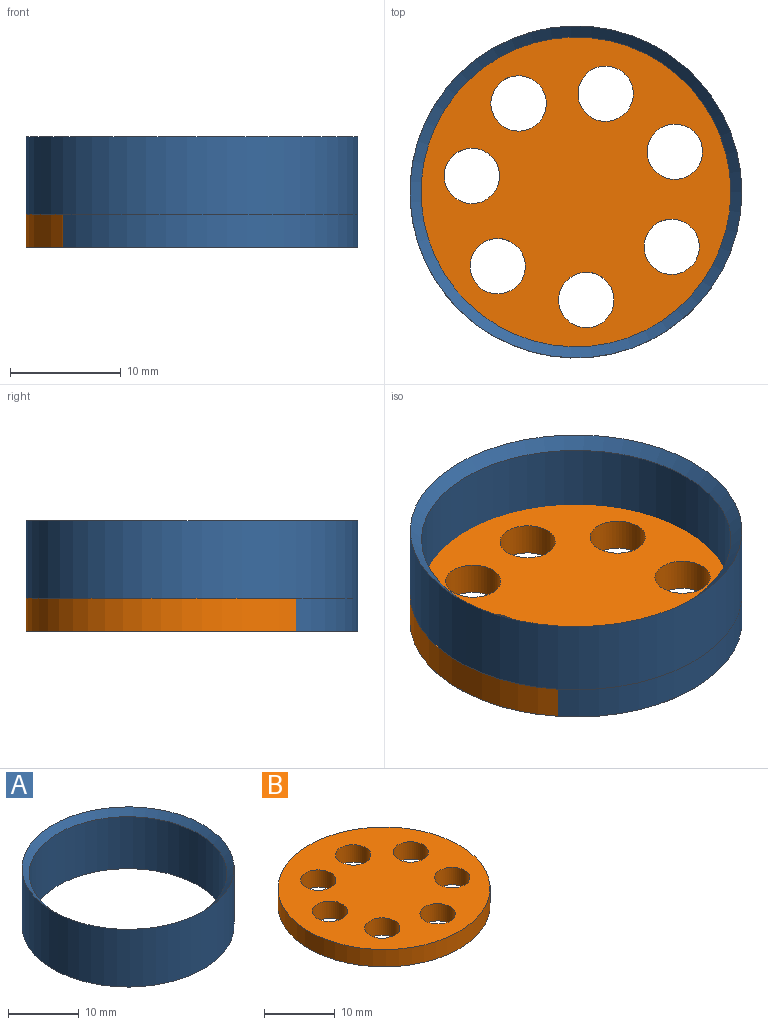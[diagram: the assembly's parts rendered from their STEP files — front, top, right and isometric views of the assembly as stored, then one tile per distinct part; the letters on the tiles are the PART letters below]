
ASSEMBLY  parts=2 mates=1
PART A: 4 faces, bbox 30x30x10 mm
  f0: cylinder r=14mm len=28mm, axis (0,0,-1), area 791.7mm2, adj f2,f3
  f1: cylinder r=15mm len=30mm, axis (0,0,-1), area 942.5mm2, adj f2,f3
  f2: plane 30x30mm, normal (0,0,-1), area 91.1mm2, adj f0,f1
  f3: cone r=14mm half-angle=45deg, axis (0,0,1), area 128.8mm2, adj f0,f1
PART B: 10 faces, bbox 30x30x3 mm
  f0: cylinder r=2.5mm len=5mm, axis (0,0,-1), area 47.1mm2, adj f8,f9
  f1: cylinder r=2.5mm len=5mm, axis (0,0,-1), area 47.1mm2, adj f8,f9
  f2: cylinder r=2.5mm len=5mm, axis (0,0,-1), area 47.1mm2, adj f8,f9
  f3: cylinder r=2.5mm len=5mm, axis (0,0,-1), area 47.1mm2, adj f8,f9
  f4: cylinder r=2.5mm len=5mm, axis (0,0,-1), area 47.1mm2, adj f8,f9
  f5: cylinder r=2.5mm len=5mm, axis (0,0,-1), area 47.1mm2, adj f8,f9
  f6: cylinder r=2.5mm len=5mm, axis (0,0,-1), area 47.1mm2, adj f8,f9
  f7: cylinder r=15mm len=30mm, axis (0,0,-1), area 282.7mm2, adj f8,f9
  f8: plane 30x30mm, normal (0,0,1), area 569.4mm2, adj f0,f1,f2,f3,f4,f5,f6,f7
  f9: plane 30x30mm, normal (0,0,-1), area 569.4mm2, adj f0,f1,f2,f3,f4,f5,f6,f7
PLACE A t=(-20.22,-17.96,7.84)mm
PLACE B t=(-46.38,38.34,7.84)mm
MATE fastened B.f9 <-> A.f0  axis (0,0,-1) through (-20.22,-17.96,7.84)mm
